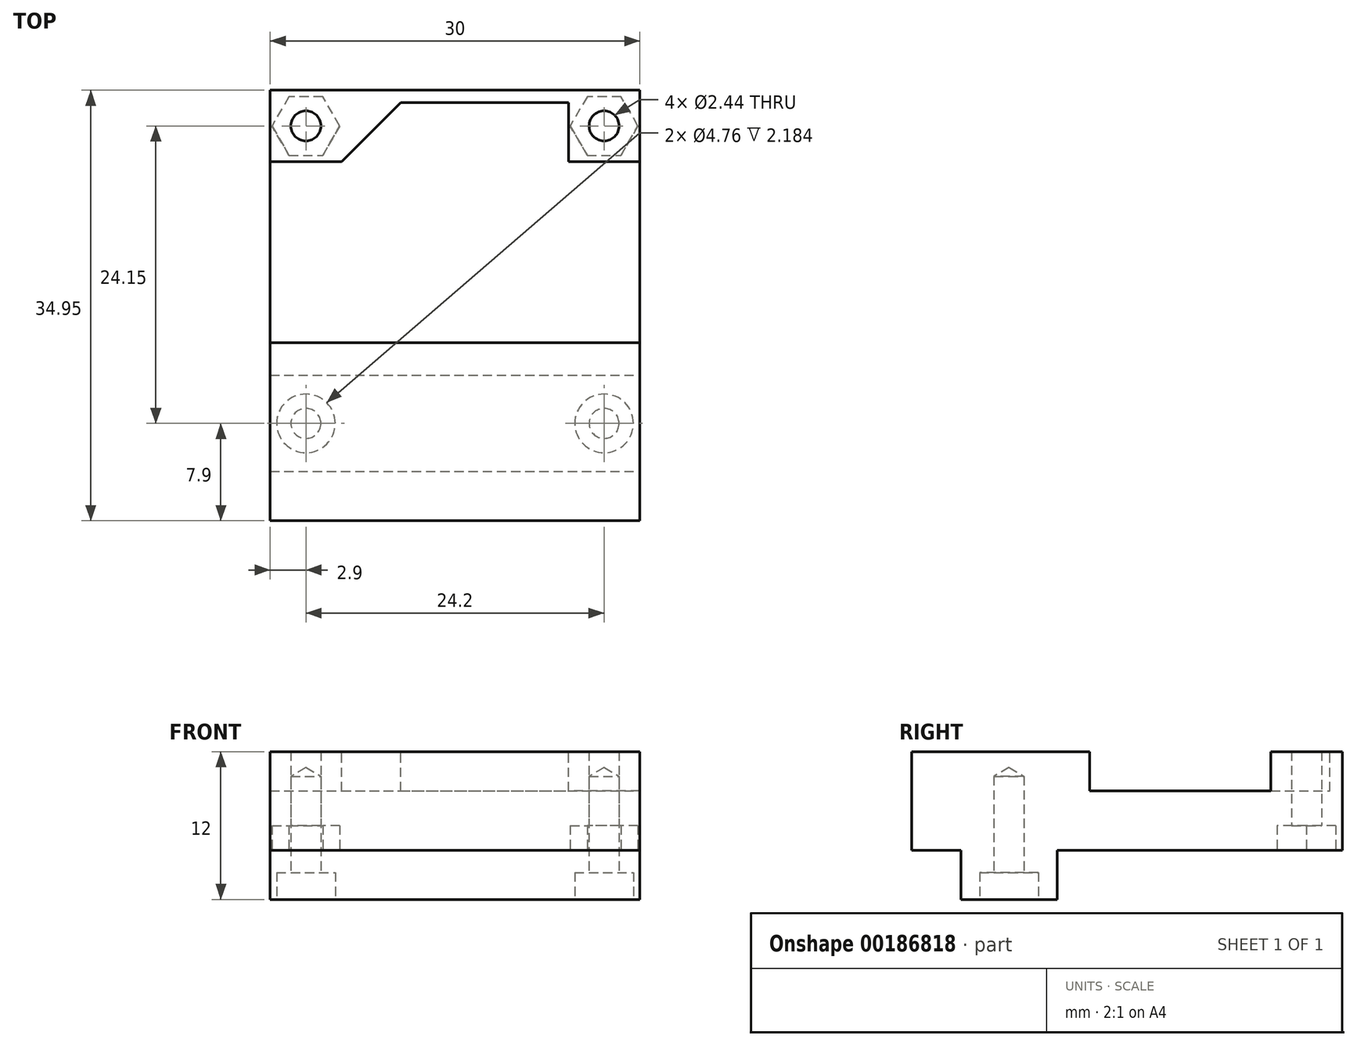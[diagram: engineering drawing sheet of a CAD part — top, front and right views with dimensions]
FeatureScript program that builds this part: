
annotation { "Feature Type Name" : "Feature", "Feature Type Description" : "" }
export const myFeature = defineFeature(function(context is Context, id is Id, definition is map)
    precondition{}
    {
        {
            var Q0;
            Q0=qCreatedBy(makeId("Top.planeOp"),FACE);
            var sketch = newSketch(context, id + "F0", { "sketchPlane" : qUnion([Q0])});
            skLineSegment(sketch, "E0.bottom", {"start": v(-15, -16) * mm, "end": v(15, -16) * mm});
            skLineSegment(sketch, "E0.top", {"start": v(-15, 34.95) * mm, "end": v(15, 34.95) * mm});
            skLineSegment(sketch, "E0.left", {"start": v(-15, -16) * mm, "end": v(-15, 34.95) * mm});
            skLineSegment(sketch, "E0.right", {"start": v(15, -16) * mm, "end": v(15, 34.95) * mm});
            skCircle(sketch, "E1", {"center": v(-12.1, 32.05) * mm, "radius": 1.3 * mm});
            skCircle(sketch, "E2", {"center": v(12.1, 32.05) * mm, "radius": 1.3 * mm});
            skCircle(sketch, "E3", {"center": v(-12.1, 7.9) * mm, "radius": 1.3 * mm});
            skCircle(sketch, "E4", {"center": v(12.1, 7.9) * mm, "radius": 1.3 * mm});
            skLineSegment(sketch, "E5", {"start": v(-15, 10.8) * mm, "end": v(15, 10.8) * mm});
            skLineSegment(sketch, "E6", {"start": v(-15, 0) * mm, "end": v(15, 0) * mm});
            skCircle(sketch, "E7.cCircle", {"center": v(-12.1, 32.05) * mm, "radius": 2.75 * mm, "construction": true});
            skLineSegment(sketch, "E7.0", {"start": v(-9.35, 32.05) * mm, "end": v(-10.73, 29.67) * mm});
            skLineSegment(sketch, "E7.1", {"start": v(-10.73, 29.67) * mm, "end": v(-13.47, 29.67) * mm});
            skLineSegment(sketch, "E7.2", {"start": v(-13.47, 29.67) * mm, "end": v(-14.85, 32.05) * mm});
            skLineSegment(sketch, "E7.3", {"start": v(-14.85, 32.05) * mm, "end": v(-13.47, 34.43) * mm});
            skLineSegment(sketch, "E7.4", {"start": v(-13.47, 34.43) * mm, "end": v(-10.73, 34.43) * mm});
            skLineSegment(sketch, "E7.5", {"start": v(-10.73, 34.43) * mm, "end": v(-9.35, 32.05) * mm});
            skCircle(sketch, "E8.cCircle", {"center": v(12.1, 32.05) * mm, "radius": 2.75 * mm, "construction": true});
            skLineSegment(sketch, "E8.0", {"start": v(9.35, 32.05) * mm, "end": v(10.73, 34.43) * mm});
            skLineSegment(sketch, "E8.1", {"start": v(10.73, 34.43) * mm, "end": v(13.47, 34.43) * mm});
            skLineSegment(sketch, "E8.2", {"start": v(13.47, 34.43) * mm, "end": v(14.85, 32.05) * mm});
            skLineSegment(sketch, "E8.3", {"start": v(14.85, 32.05) * mm, "end": v(13.47, 29.67) * mm});
            skLineSegment(sketch, "E8.4", {"start": v(13.47, 29.67) * mm, "end": v(10.73, 29.67) * mm});
            skLineSegment(sketch, "E8.5", {"start": v(10.73, 29.67) * mm, "end": v(9.35, 32.05) * mm});
            skLineSegment(sketch, "E9", {"start": v(-15, 4) * mm, "end": v(15, 4) * mm});
            skLineSegment(sketch, "E10", {"start": v(-15, 11.8) * mm, "end": v(15, 11.8) * mm});
            skLineSegment(sketch, "E11", {"start": v(-12.1, 7.9) * mm, "end": v(12.1, 7.9) * mm, "construction": true});
            skSolve(sketch);
        }
        {
            var Q0;
            {var subQ0=sQuery(id+"F0.wireOp",EDGE,"E0.top");Q0=makeQuery(id+"F0.imprint","IMPRINT",FACE,{"disambiguationData":[TD([[makeQuery(id+"F0.imprint","IMPRINT",EDGE,{"derivedFrom":subQ0}),-1.0]])]});}
            var Q1;
            Q1=makeQuery(id+"F0.imprint","IMPRINT",FACE,{"disambiguationData":[TD([[makeQuery(id+"F0.imprint","IMPRINT",EDGE,{"derivedFrom":sQuery(id+"F0.wireOp",EDGE,"E1")}),1.0]])]});
            var Q2;
            Q2=makeQuery(id+"F0.imprint","IMPRINT",FACE,{"disambiguationData":[TD([[makeQuery(id+"F0.imprint","IMPRINT",EDGE,{"derivedFrom":sQuery(id+"F0.wireOp",EDGE,"E2")}),1.0]])]});
            var Q3;
            Q3=makeQuery(id+"F0.imprint","IMPRINT",FACE,{"disambiguationData":[TD([[makeQuery(id+"F0.imprint","IMPRINT",EDGE,{"derivedFrom":sQuery(id+"F0.wireOp",EDGE,"E4")}),1.0]])]});
            var Q4;
            Q4=makeQuery(id+"F0.imprint","IMPRINT",FACE,{"disambiguationData":[TD([[makeQuery(id+"F0.imprint","IMPRINT",EDGE,{"derivedFrom":sQuery(id+"F0.wireOp",EDGE,"E3")}),1.0]])]});
            var Q5;
            Q5=makeQuery(id+"F0.imprint","IMPRINT",FACE,{"disambiguationData":[TD([[makeQuery(id+"F0.imprint","IMPRINT",EDGE,{"derivedFrom":sQuery(id+"F0.wireOp",EDGE,"E3")}),-1.0]])]});
            var Q6;
            Q6=makeQuery(id+"F0.imprint","IMPRINT",FACE,{"disambiguationData":[TD([[makeQuery(id+"F0.imprint","IMPRINT",EDGE,{"derivedFrom":sQuery(id+"F0.wireOp",EDGE,"E1")}),-1.0]])]});
            var Q7;
            Q7=makeQuery(id+"F0.imprint","IMPRINT",FACE,{"disambiguationData":[TD([[makeQuery(id+"F0.imprint","IMPRINT",EDGE,{"derivedFrom":sQuery(id+"F0.wireOp",EDGE,"E2")}),-1.0]])]});
            var Q8;
            {var subQ0=sQuery(id+"F0.wireOp",EDGE,"E5");Q8=makeQuery(id+"F0.imprint","IMPRINT",FACE,{"disambiguationData":[TD([[makeQuery(id+"F0.imprint","IMPRINT",EDGE,{"derivedFrom":subQ0}),1.0]])]});}
            var Q9;
            {var subQ0=sQuery(id+"F0.wireOp",EDGE,"E6");Q9=makeQuery(id+"F0.imprint","IMPRINT",FACE,{"disambiguationData":[TD([[makeQuery(id+"F0.imprint","IMPRINT",EDGE,{"derivedFrom":subQ0}),1.0]])]});}
            extrude(context, id + "F1", {"entities" : qUnion([Q0, Q1, Q2, Q3, Q4, Q5, Q6, Q7, Q8, Q9]), "depth" : 12 * mm});
        }
        {
            var Q0;
            Q0=makeQuery(id+"F1.opExtrude","CAP_FACE",FACE,{"disambiguationData":[OSD([sQuery(id+"F0.wireOp",EDGE,"E0.top"),sQuery(id+"F0.wireOp",EDGE,"E0.left"),sQuery(id+"F0.wireOp",EDGE,"E0.right"),sQuery(id+"F0.wireOp",EDGE,"E6")])],"isStart":false});
            var sketch = newSketch(context, id + "F2", { "sketchPlane" : qUnion([Q0])});
            skLineSegment(sketch, "E12.0.3", {"start": v(15, 10.8) * mm, "end": v(-15, 10.8) * mm});
            skLineSegment(sketch, "E13.bottom", {"start": v(-15, 10.8) * mm, "end": v(15, 10.8) * mm});
            skLineSegment(sketch, "E13.top", {"start": v(-15, 11.8) * mm, "end": v(15, 11.8) * mm});
            skLineSegment(sketch, "E13.left", {"start": v(-15, 10.8) * mm, "end": v(-15, 11.8) * mm});
            skLineSegment(sketch, "E13.right", {"start": v(15, 10.8) * mm, "end": v(15, 11.8) * mm});
            skLineSegment(sketch, "E14.bottom", {"start": v(-15, 34.95) * mm, "end": v(-9.2, 34.95) * mm});
            skLineSegment(sketch, "E14.top", {"start": v(-15, 29.15) * mm, "end": v(-9.2, 29.15) * mm});
            skLineSegment(sketch, "E14.left", {"start": v(-15, 34.95) * mm, "end": v(-15, 29.15) * mm});
            skLineSegment(sketch, "E14.right", {"start": v(-9.2, 34.95) * mm, "end": v(-9.2, 29.15) * mm});
            skLineSegment(sketch, "E15.bottom", {"start": v(15, 34.95) * mm, "end": v(9.2, 34.95) * mm});
            skLineSegment(sketch, "E15.top", {"start": v(15, 29.15) * mm, "end": v(9.2, 29.15) * mm});
            skLineSegment(sketch, "E15.left", {"start": v(15, 34.95) * mm, "end": v(15, 29.15) * mm});
            skLineSegment(sketch, "E15.right", {"start": v(9.2, 34.95) * mm, "end": v(9.2, 29.15) * mm});
            skLineSegment(sketch, "E16.bottom", {"start": v(-15, 20.25) * mm, "end": v(-9.2, 20.25) * mm});
            skLineSegment(sketch, "E16.top", {"start": v(-15, 14.45) * mm, "end": v(-9.2, 14.45) * mm});
            skLineSegment(sketch, "E16.left", {"start": v(-15, 20.25) * mm, "end": v(-15, 14.45) * mm});
            skLineSegment(sketch, "E16.right", {"start": v(-9.2, 20.25) * mm, "end": v(-9.2, 14.45) * mm});
            skLineSegment(sketch, "E17.bottom", {"start": v(15, 20.25) * mm, "end": v(9.2, 20.25) * mm});
            skLineSegment(sketch, "E17.top", {"start": v(15, 14.45) * mm, "end": v(9.2, 14.45) * mm});
            skLineSegment(sketch, "E17.left", {"start": v(15, 20.25) * mm, "end": v(15, 14.45) * mm});
            skLineSegment(sketch, "E17.right", {"start": v(9.2, 20.25) * mm, "end": v(9.2, 14.45) * mm});
            skLineSegment(sketch, "E18", {"start": v(-15, 17.35) * mm, "end": v(15, 17.35) * mm, "construction": true});
            skLineSegment(sketch, "E19.bottom", {"start": v(-15, 10.8) * mm, "end": v(-9.2, 10.8) * mm});
            skLineSegment(sketch, "E19.top", {"start": v(-15, 5) * mm, "end": v(-9.2, 5) * mm});
            skLineSegment(sketch, "E19.left", {"start": v(-15, 10.8) * mm, "end": v(-15, 5) * mm});
            skLineSegment(sketch, "E19.right", {"start": v(-9.2, 10.8) * mm, "end": v(-9.2, 5) * mm});
            skLineSegment(sketch, "E20.bottom", {"start": v(15, 10.8) * mm, "end": v(9.2, 10.8) * mm});
            skLineSegment(sketch, "E20.top", {"start": v(15, 5) * mm, "end": v(9.2, 5) * mm});
            skLineSegment(sketch, "E20.left", {"start": v(15, 10.8) * mm, "end": v(15, 5) * mm});
            skLineSegment(sketch, "E20.right", {"start": v(9.2, 10.8) * mm, "end": v(9.2, 5) * mm});
            skLineSegment(sketch, "E21", {"start": v(-15, 7.9) * mm, "end": v(15, 7.9) * mm, "construction": true});
            skLineSegment(sketch, "E22", {"start": v(-9.2, 14.45) * mm, "end": v(9.2, 14.45) * mm});
            skLineSegment(sketch, "E23.0.0", {"start": v(15, 34.95) * mm, "end": v(-15, 34.95) * mm});
            skLineSegment(sketch, "E23.0.1", {"start": v(-15, 34.95) * mm, "end": v(-15, 0) * mm});
            skLineSegment(sketch, "E23.0.2", {"start": v(-15, 0) * mm, "end": v(15, 0) * mm});
            skLineSegment(sketch, "E23.0.3", {"start": v(15, 0) * mm, "end": v(15, 34.95) * mm});
            skLineSegment(sketch, "E24.0.0", {"start": v(-15, 0) * mm, "end": v(-15, -16) * mm, "construction": true});
            skLineSegment(sketch, "E24.0.1", {"start": v(-15, -16) * mm, "end": v(15, -16) * mm, "construction": true});
            skLineSegment(sketch, "E24.0.2", {"start": v(15, -16) * mm, "end": v(15, 0) * mm, "construction": true});
            skLineSegment(sketch, "E24.0.3", {"start": v(15, 0) * mm, "end": v(-15, 0) * mm, "construction": true});
            skLineSegment(sketch, "E25", {"start": v(-15, 23.35) * mm, "end": v(-3.4, 34.95) * mm});
            skLineSegment(sketch, "E26", {"start": v(-15, 13.45) * mm, "end": v(15, 13.45) * mm});
            skLineSegment(sketch, "E27", {"start": v(-15, 26.05) * mm, "end": v(-2.4, 13.45) * mm});
            skLineSegment(sketch, "E28", {"start": v(-9.2, 33.95) * mm, "end": v(9.2, 33.95) * mm});
            skSolve(sketch);
        }
        {
            var Q0;
            Q0=makeQuery(id+"F2.imprint","IMPRINT",FACE,{"disambiguationData":[TD([[makeQuery(id+"F2.imprint","IMPRINT",EDGE,{"derivedFrom":sQuery(id+"F2.wireOp",EDGE,"E12.0.0")}),-1.0]])]});
            var Q1;
            Q1=makeQuery(id+"F2.imprint","IMPRINT",FACE,{"disambiguationData":[TD([[makeQuery(id+"F2.imprint","IMPRINT",EDGE,{"derivedFrom":sQuery(id+"F2.wireOp",EDGE,"E13.bottom")}),1.0]])]});
            var Q2;
            Q2=makeQuery(id+"F2.imprint","IMPRINT",FACE,{"disambiguationData":[TD([[makeQuery(id+"F2.imprint","IMPRINT",EDGE,{"derivedFrom":sQuery(id+"F2.wireOp",EDGE,"E20.bottom")}),1.0]])]});
            var Q3;
            Q3=makeQuery(id+"F2.imprint","IMPRINT",FACE,{"disambiguationData":[TD([[makeQuery(id+"F2.imprint","IMPRINT",EDGE,{"derivedFrom":sQuery(id+"F2.wireOp",EDGE,"E19.bottom")}),-1.0]])]});
            var Q4;
            Q4=makeQuery(id+"F2.imprint","IMPRINT",FACE,{"disambiguationData":[TD([[makeQuery(id+"F2.imprint","IMPRINT",EDGE,{"derivedFrom":sQuery(id+"F2.wireOp",EDGE,"E13.bottom")}),-1.0]])]});
            var Q5;
            {var subQ12=sQuery(id+"F2.wireOp",EDGE,"E15.top");Q5=makeQuery(id+"F2.imprint","IMPRINT",FACE,{"disambiguationData":[TD([[makeQuery(id+"F2.imprint","IMPRINT",EDGE,{"derivedFrom":subQ12}),1.0]])]});}
            var Q6;
            {var subQ0=sQuery(id+"F2.wireOp",EDGE,"E16.bottom");Q6=makeQuery(id+"F2.imprint","IMPRINT",FACE,{"disambiguationData":[TD([[makeQuery(id+"F2.imprint","IMPRINT",EDGE,{"derivedFrom":subQ0}),1.0]])]});}
            var Q7;
            {var subQ0=sQuery(id+"F2.wireOp",EDGE,"E14.top");Q7=makeQuery(id+"F2.imprint","IMPRINT",FACE,{"disambiguationData":[TD([[makeQuery(id+"F2.imprint","IMPRINT",EDGE,{"derivedFrom":subQ0}),-1.0]])]});}
            var Q8;
            {var subQ0=sQuery(id+"F2.wireOp",EDGE,"E25");var subQ1=sQuery(id+"F2.wireOp",EDGE,"E23.0.1");var subQ2=makeQuery(id+"F2.imprint","INTERSECT",VERTEX,{"derivedFrom":[subQ1,subQ0]});Q8=makeQuery(id+"F2.imprint","IMPRINT",FACE,{"disambiguationData":[TD([[makeQuery(id+"F2.imprint","IMPRINT",EDGE,{"disambiguationData":[TD([[subQ2,-1.0]])],"derivedFrom":subQ1}),-1.0]])]});}
            var Q9;
            {var subQ0=sQuery(id+"F2.wireOp",EDGE,"E16.right");Q9=makeQuery(id+"F2.imprint","IMPRINT",FACE,{"disambiguationData":[TD([[makeQuery(id+"F2.imprint","IMPRINT",EDGE,{"derivedFrom":subQ0}),1.0]])]});}
            var Q10;
            {var subQ0=sQuery(id+"F2.wireOp",EDGE,"E16.bottom");Q10=makeQuery(id+"F2.imprint","IMPRINT",FACE,{"disambiguationData":[TD([[makeQuery(id+"F2.imprint","IMPRINT",EDGE,{"derivedFrom":subQ0}),-1.0]])]});}
            var Q11;
            {var subQ0=sQuery(id+"F2.wireOp",EDGE,"E17.bottom");Q11=makeQuery(id+"F2.imprint","IMPRINT",FACE,{"disambiguationData":[TD([[makeQuery(id+"F2.imprint","IMPRINT",EDGE,{"derivedFrom":subQ0}),1.0]])]});}
            extrude(context, id + "F3", {"entities" : qUnion([Q0, Q1, Q2, Q3, Q4, Q5, Q6, Q7, Q8, Q9, Q10, Q11]), "operationType" : NewBodyOperationType.REMOVE, "oppositeDirection" : true, "depth" : 3.2 * mm});
        }
        {
            var Q0;
            {var subQ0=sQuery(id+"F0.wireOp",EDGE,"E0.top");Q0=makeQuery(id+"F0.imprint","IMPRINT",FACE,{"disambiguationData":[TD([[makeQuery(id+"F0.imprint","IMPRINT",EDGE,{"derivedFrom":subQ0}),-1.0]])]});}
            var Q1;
            Q1=makeQuery(id+"F0.imprint","IMPRINT",FACE,{"disambiguationData":[TD([[makeQuery(id+"F0.imprint","IMPRINT",EDGE,{"derivedFrom":sQuery(id+"F0.wireOp",EDGE,"E1")}),-1.0]])]});
            var Q2;
            Q2=makeQuery(id+"F0.imprint","IMPRINT",FACE,{"disambiguationData":[TD([[makeQuery(id+"F0.imprint","IMPRINT",EDGE,{"derivedFrom":sQuery(id+"F0.wireOp",EDGE,"E1")}),1.0]])]});
            var Q3;
            Q3=makeQuery(id+"F0.imprint","IMPRINT",FACE,{"disambiguationData":[TD([[makeQuery(id+"F0.imprint","IMPRINT",EDGE,{"derivedFrom":sQuery(id+"F0.wireOp",EDGE,"E2")}),1.0]])]});
            var Q4;
            Q4=makeQuery(id+"F0.imprint","IMPRINT",FACE,{"disambiguationData":[TD([[makeQuery(id+"F0.imprint","IMPRINT",EDGE,{"derivedFrom":sQuery(id+"F0.wireOp",EDGE,"E2")}),-1.0]])]});
            var Q5;
            {var subQ0=sQuery(id+"F0.wireOp",EDGE,"E6");Q5=makeQuery(id+"F0.imprint","IMPRINT",FACE,{"disambiguationData":[TD([[makeQuery(id+"F0.imprint","IMPRINT",EDGE,{"derivedFrom":subQ0}),1.0]])]});}
            extrude(context, id + "F4", {"entities" : qUnion([Q0, Q1, Q2, Q3, Q4, Q5]), "operationType" : NewBodyOperationType.REMOVE, "depth" : 4 * mm});
        }
        {
            var Q0;
            Q0=sQuery(id+"F0.wireOp",VERTEX,"E3.center");
            var Q1;
            Q1=sQuery(id+"F0.wireOp",VERTEX,"E4.center");
            var Q2;
            Q2=makeQuery(id+"F1.opExtrude","SWEPT_BODY",BODY,{"disambiguationData":[OSD([sQuery(id+"F0.wireOp",EDGE,"E0.top"),sQuery(id+"F0.wireOp",EDGE,"E0.left"),sQuery(id+"F0.wireOp",EDGE,"E0.right"),sQuery(id+"F0.wireOp",EDGE,"E6")])]});
            hole(context, id + "F5", {"style" : HoleStyle.C_BORE, "endStyle" : HoleEndStyle.BLIND, "oppositeDirection" : true, "standardTappedOrClearance" : lookupTablePath({ "standard" : "ANSI", "fit" : "Normal (ASME)", "size" : "#2", "type" : "Clearance" }), "standardBlindInLast" : lookupTablePath({ "fit" : "Free", "standard" : "ANSI", "size" : "#2", "type" : "Clearance" }), "holeDiameter" : 2.44 * mm, "cBoreDiameter" : 4.76 * mm, "cBoreDepth" : 2.18 * mm, "holeDepth" : 10 * mm, "locations" : qUnion([Q0, Q1]), "scope" : qUnion([Q2])});
        }
        {
            var Q0;
            Q0=sQuery(id+"F0.wireOp",VERTEX,"E1.center");
            var Q1;
            Q1=sQuery(id+"F0.wireOp",VERTEX,"E2.center");
            var Q2;
            Q2=makeQuery(id+"F1.opExtrude","SWEPT_BODY",BODY,{"disambiguationData":[OSD([sQuery(id+"F0.wireOp",EDGE,"E0.top"),sQuery(id+"F0.wireOp",EDGE,"E0.left"),sQuery(id+"F0.wireOp",EDGE,"E0.right"),sQuery(id+"F0.wireOp",EDGE,"E6")])]});
            hole(context, id + "F6", {"style" : HoleStyle.SIMPLE, "endStyle" : HoleEndStyle.BLIND, "oppositeDirection" : true, "standardTappedOrClearance" : lookupTablePath({ "standard" : "ANSI", "fit" : "Normal (ASME)", "size" : "#2", "type" : "Clearance" }), "standardBlindInLast" : lookupTablePath({ "fit" : "Free", "standard" : "ANSI", "size" : "#2", "type" : "Clearance" }), "holeDiameter" : 2.44 * mm, "holeDepth" : 20 * mm, "locations" : qUnion([Q0, Q1]), "scope" : qUnion([Q2])});
        }
        {
            var Q0;
            Q0=makeQuery(id+"F0.imprint","IMPRINT",FACE,{"disambiguationData":[TD([[makeQuery(id+"F0.imprint","IMPRINT",EDGE,{"derivedFrom":sQuery(id+"F0.wireOp",EDGE,"E1")}),-1.0]])]});
            var Q1;
            Q1=makeQuery(id+"F0.imprint","IMPRINT",FACE,{"disambiguationData":[TD([[makeQuery(id+"F0.imprint","IMPRINT",EDGE,{"derivedFrom":sQuery(id+"F0.wireOp",EDGE,"E2")}),-1.0]])]});
            var Q2;
            Q2=makeQuery(id+"F0.imprint","IMPRINT",FACE,{"disambiguationData":[TD([[makeQuery(id+"F0.imprint","IMPRINT",EDGE,{"derivedFrom":sQuery(id+"F0.wireOp",EDGE,"E2")}),1.0]])]});
            var Q3;
            Q3=makeQuery(id+"F0.imprint","IMPRINT",FACE,{"disambiguationData":[TD([[makeQuery(id+"F0.imprint","IMPRINT",EDGE,{"derivedFrom":sQuery(id+"F0.wireOp",EDGE,"E1")}),1.0]])]});
            extrude(context, id + "F7", {"entities" : qUnion([Q0, Q1, Q2, Q3]), "operationType" : NewBodyOperationType.REMOVE, "depth" : 6 * mm});
        }
    });
